# Revit family: Cartel de extinción óptico-acústico exterior_Aguilera Electronica
name_source: partatom
category: Dispositivos de alarma de incendios
revit_build: Autodesk Revit 2017 (Build: 20160225_1515(x64)
units: mm (PartAtom-declared; Revit-internal decimal feet)

## family parameters
Anfitrión = Cara
Compartido = No
Corte con vacíos al cargar = No
Cota de conector redondo = Diámetro de uso
Mantener orientación de anotación = Sí
Número OmniClass = 23.85.30.21.11.17
Punto de cálculo de habitación = No
Tipo de pieza = Normal
Título OmniClass = Other Components

## types (1)
- Cartel de extinción óptico-acústico para uso exterior
    Descripción = Indicado para exteriores, IP65.

Se suministran con dos letreros adhesivos: EXTINCION DISPARADA – FUEGO.
Se puede seleccionar el sonido fijo, intermitente o sin sonido y la iluminación fija o intermitente.
Material ABS. Consumo 95mA /24Vcc. Intensidad sonora: 108dB /1m.
Dimensiones: 365x 180x50mm.
    Diámetro tubo = 20 mm  [stored 0.0656168 ft]
    Elevación por defecto = 1200 mm
    Fabricante = Aguilera Electrónica
    Modelo = AE/V-CEIP
    Símbolo = Sí
    Símbolo texto modelo = Sí
    URL = https://aguilera.es

note: [stored X ft] marks values corroborated as IEEE doubles in the binary element streams (Revit-internal decimal feet)
